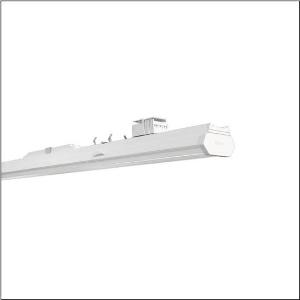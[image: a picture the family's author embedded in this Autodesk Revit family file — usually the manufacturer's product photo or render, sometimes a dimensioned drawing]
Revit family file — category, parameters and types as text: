
# Revit family: licross_21_protected_mo_52tp12cn49xg
name_source: partatom
category: Lighting Fixtures
units: mm (PartAtom-declared; Revit-internal decimal feet)

## family parameters
Cut with Voids When Loaded = No
Host = Face
Light Source = No
Part Type = Normal
Room Calculation Point = No
Round Connector Dimension = Use Diameter
Shared = No

## types (1)
- --- (1 x LED, 9110 lm, 50.4 W, 4000K)
    Apparent Load = 50 VA
    CIE Flux Codes = 73 92 98 99 100
    Color Rendering = 80
    Color Temperature = 4000K
    Default Elevation = 1800 mm
    Description = Licross 21 Protected MO, luminaire insert, of sheet steel, galvanised, coil coated, white, length: 1.500mm, width: 90mm, height: 103mm, LED rated luminous flux: 9.120lm, light colour: 840, SDCM (Standard Deviation of Colour Matching)MacAdam ≤ 3 SDCM (initial), control gear: ON/OFF Multilumen, CLOi, with plug, 3-pole, with phase selection, mains connection: 220..240V, AC, 50/60Hz, start of lifetime: 50W, end of service life: 61W, internal wiring halogen-free, primary light control with lens, of plastic, primary optical cover: cover, of PMMA, light emission: direct distribution, primary light characteristic: symmetric, protection rating (complete): IP64, insulation class (complete): insulation class I (protective earthing), certification: CE, ENEC, VDE, UKCA, protection symbol: D if used in an environment with conductive dust loads with corresponding accessories, impact resistance: IK06, permissible ambient temperature for indoor applications: -35..+45°C, corresponds to IFS (International Featured Standards) requirements for safety and quality in the food industry, reducing of maximum allowable ambient temperature of 5°C with ceiling mounting, LABS conformity tested according to VDMA 24364:2018-05, The light source and the operating device comply with the requirements of the Ecodesign Regulation (EU) 2019/2020 and are replaceable in accordance with this regulation, packaging unit: 1 piece
    Height = 92 mm
    Lamp = 1 x LED
    Lamp Light Flux = 9110 lm
    Lamp Power = 50.4 W
    Lamp count = 1
    Length = 1500 mm
    Luminous efficacy = 181 lm/W
    Manufacturer = Siteco
    ModVariant = No
    Model = 52TP12CN49XG
    Mounting Place = Ceiling
    Mounting Type = Pendant
    Number of Poles = 1
    OnlyDefault = Yes
    Power Factor = 1
    Product Name = Licross 21 Protected MO
    Product group = luminaire insert | ceiling pendant
    ProductGroupID = 901
    Protection Class = Protection class I
    Protection Degree = IP 64
    RLX_Detail_Level = 1
    RLX_Emergency_Light_Flux = 0 lm
    RLX_Emergency_Type = 0
    RLX_Emergency_Type_DB = No
    RlxData = <blob elided: 22505 chars, md5=565a6c42>
    Socket = socket
    Standby Power = 0 W
    System Light Flux = 9110 lm
    System Power = 50 W
    Type Comments = factory setting: luminous flux: 100 % | (A | C | E) | 117 mA
    Type Image = l_1256148.jpg
    URL = http://relux.com
    VarID = @adj_112693
    Voltage = 0 V
    Weight = 0.00 kg
    Width = 88 mm

## geometry (parser evidence)
native form markers: Blend x4, Sweep x12
no freeform markers — native parametric forms only
